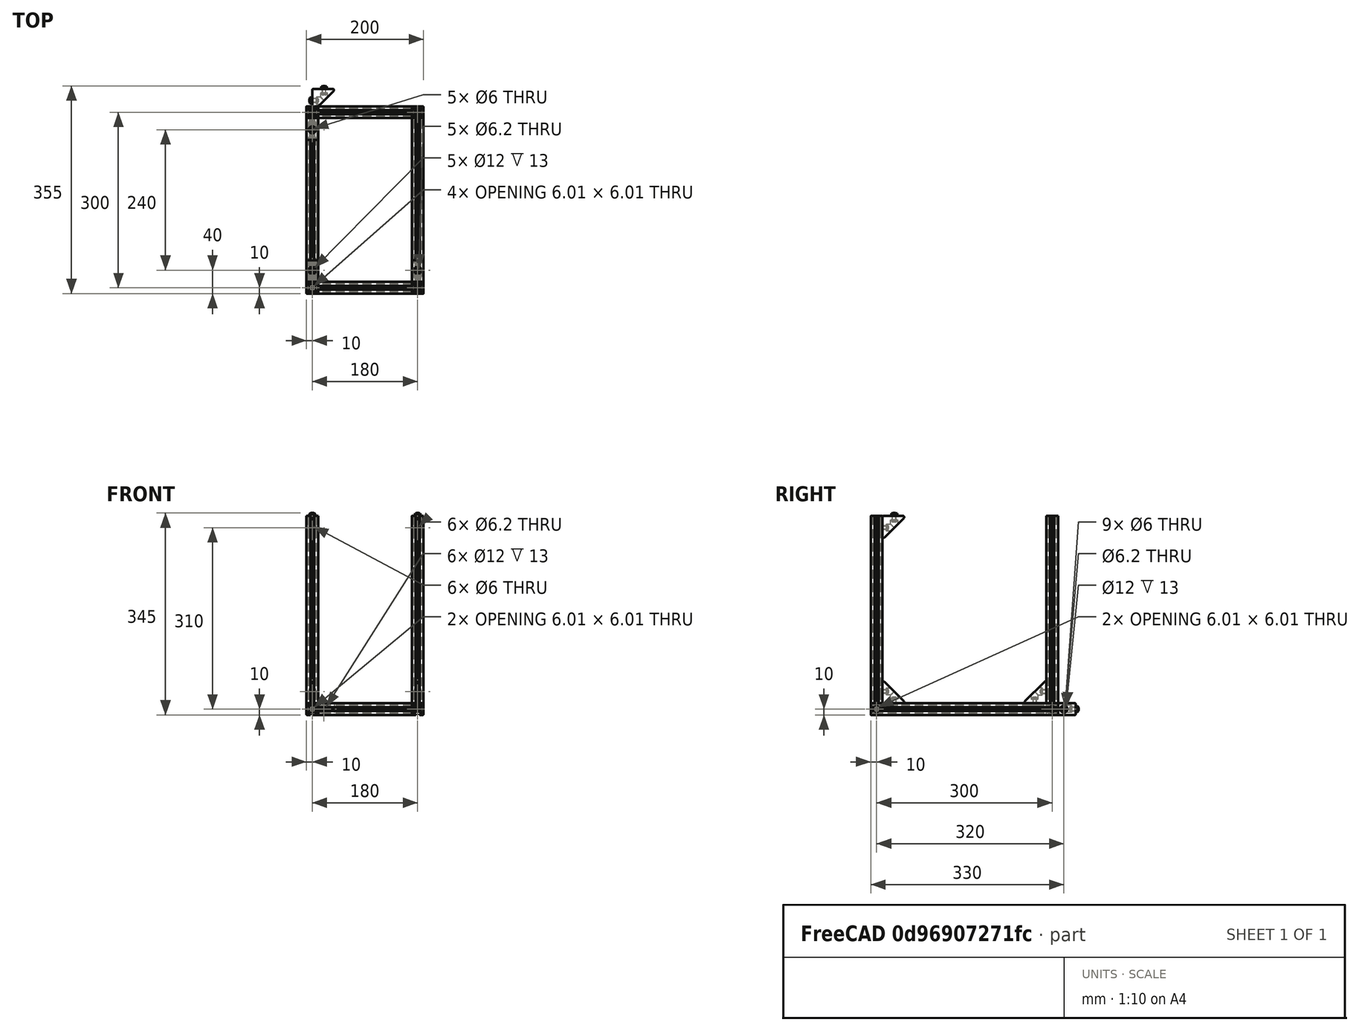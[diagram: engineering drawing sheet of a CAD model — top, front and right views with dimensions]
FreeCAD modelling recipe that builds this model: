
FCSTD DOCUMENT  (FreeCAD 0.17R9796 (Git))
Label: rawframeNG2b
License: All rights reserved
LicenseURL: http://en.wikipedia.org/wiki/All_rights_reserved
objects: Part::Feature×49, Part::FeaturePython×16, App::Part×6, Part::Compound×5
note: 70 computed .brp shape members not serialized (recipe doc carries the construction recipe); baked Part::Feature solids carry a one-line shape summary decoded from their .brp

FEATURE [Part::Feature] Pocket003001  label="tslot32con"
  Placement = pos=(0,10,10) rot=(1,0,0;1.5708rad)
  shape: bbox 20 x 320 x 20 mm, 150 faces (baked)
FEATURE [Part::Feature] Pocket003002  label="tslot16"
  Placement = pos=(10,0,10) rot=(0,1,0;1.5708rad)
  shape: bbox 160 x 20 x 20 mm, 94 faces (baked)
FEATURE [Part::Feature] Pocket003006  label="tslot16_001"
  Placement = pos=(10,-300,10) rot=(0,1,0;1.5708rad)
  shape: bbox 160 x 20 x 20 mm, 94 faces (baked)
FEATURE [Part::Feature] Pocket003007  label="tslot32con_001"
  Placement = pos=(180,-310,10) rot=(0,0.707107,0.707107;3.14159rad)
  shape: bbox 20 x 320 x 20 mm, 150 faces (baked)
FEATURE [Part::FeaturePython] Screw  label="M6x25-Screw"  # Fasteners workbench fastener (typed FeaturePython)
  Placement = pos=(-4,0,10) rot=(0,-1,0;1.5708rad)
  diameter = 7
  invert = false
  length = 6
  matchOuter = false
  offset = 0
  thread = false
  type = 15
FEATURE [Part::FeaturePython] Screw001  label="M6x25-Screw004"  # Fasteners workbench fastener (typed FeaturePython)
  Placement = pos=(-4,-300,10) rot=(0,-1,0;1.5708rad)
  diameter = 7
  invert = false
  length = 6
  matchOuter = false
  offset = 0
  thread = false
  type = 15
FEATURE [Part::FeaturePython] Screw002  label="M6x25-Screw005"  # Fasteners workbench fastener (typed FeaturePython)
  Placement = pos=(184,0,10) rot=(0,1,0;1.5708rad)
  diameter = 7
  invert = false
  length = 6
  matchOuter = false
  offset = 0
  thread = false
  type = 15
FEATURE [Part::FeaturePython] Screw004  label="M6x25-Screw006"  # Fasteners workbench fastener (typed FeaturePython)
  Placement = pos=(184,-300,10) rot=(0,1,0;1.5708rad)
  diameter = 7
  invert = false
  length = 6
  matchOuter = false
  offset = 0
  thread = false
  type = 15
FEATURE [App::Part] Part  label="lower_frame"
  Group = -> [Pocket003001,Pocket003002,Pocket003006,Pocket003007,Screw,Screw001,Screw002,Screw004]
  License = CC BY 3.0
  LicenseURL = http://creativecommons.org/licenses/by/3.0/
  Origin = -> PartOrigin
FEATURE [Part::Feature] Pocket003008  label="tslot32con001"
  Placement = pos=(0,10,10) rot=(1,0,0;1.5708rad)
  shape: bbox 20 x 320 x 20 mm, 150 faces (baked)
FEATURE [Part::Feature] Pocket003009  label="tslot041"
  Placement = pos=(10,0,10) rot=(0,1,0;1.5708rad)
  shape: bbox 160 x 20 x 20 mm, 94 faces (baked)
FEATURE [Part::Feature] Pocket003010  label="tslot16_002"
  Placement = pos=(10,-300,10) rot=(0,1,0;1.5708rad)
  shape: bbox 160 x 20 x 20 mm, 94 faces (baked)
FEATURE [Part::Feature] Pocket003011  label="tslot32con_002"
  Placement = pos=(180,-310,10) rot=(0,0.707107,0.707107;3.14159rad)
  shape: bbox 20 x 320 x 20 mm, 150 faces (baked)
FEATURE [Part::FeaturePython] Screw005  label="M6x25-Screw007"  # Fasteners workbench fastener (typed FeaturePython)
  Placement = pos=(-4,0,10) rot=(0,-1,0;1.5708rad)
  diameter = 7
  invert = false
  length = 6
  matchOuter = false
  offset = 0
  thread = false
  type = 15
FEATURE [Part::FeaturePython] Screw006  label="M6x25-Screw008"  # Fasteners workbench fastener (typed FeaturePython)
  Placement = pos=(-4,-300,10) rot=(0,-1,0;1.5708rad)
  diameter = 7
  invert = false
  length = 6
  matchOuter = false
  offset = 0
  thread = false
  type = 15
FEATURE [Part::FeaturePython] Screw007  label="M6x25-Screw009"  # Fasteners workbench fastener (typed FeaturePython)
  Placement = pos=(184,0,10) rot=(0,1,0;1.5708rad)
  diameter = 7
  invert = false
  length = 6
  matchOuter = false
  offset = 0
  thread = false
  type = 15
FEATURE [Part::FeaturePython] Screw008  label="M6x25-Screw010"  # Fasteners workbench fastener (typed FeaturePython)
  Placement = pos=(184,-300,10) rot=(0,1,0;1.5708rad)
  diameter = 7
  invert = false
  length = 6
  matchOuter = false
  offset = 0
  thread = false
  type = 15
FEATURE [App::Part] Part001  label="upper_frame"
  Group = -> [Pocket003008,Pocket003009,Pocket003010,Pocket003011,Screw005,Screw006,Screw007,Screw008]
  License = CC BY 3.0
  LicenseURL = http://creativecommons.org/licenses/by/3.0/
  Origin = -> PartOrigin001
  Placement = pos=(0,0,340) rot=(0,0,1;0rad)
FEATURE [Part::Feature] Fillet004001  label="Fillet005"
  shape: bbox 37.5 x 37.5 x 20 mm, 26 faces (baked)
FEATURE [Part::FeaturePython] Screw009  label="M6x12-Screw"  # Fasteners workbench fastener (typed FeaturePython)
  Placement = pos=(7,20,10) rot=(0,1,0;1.5708rad)
  diameter = 4
  invert = false
  length = 1
  matchOuter = false
  offset = 0
  thread = false
  type = 20
FEATURE [Part::Feature] Body001  label="m6nutplate"
  Placement = pos=(-1.5,15,5) rot=(0,-1,0;1.5708rad)
  shape: bbox 3 x 10 x 10 mm, 9 faces (baked)
FEATURE [App::Part] Part002  label="cornerstonescrewnut"
  License = CC BY 3.0
  LicenseURL = http://creativecommons.org/licenses/by/3.0/
  Origin = -> PartOrigin002
  Placement = pos=(10,-50,20) rot=(0,-1,0;1.5708rad)
FEATURE [Part::FeaturePython] Screw010  label="M6x12-Screw001"  # Fasteners workbench fastener (typed FeaturePython)
  Placement = pos=(20,33,10) rot=(1,0,0;1.5708rad)
  diameter = 4
  invert = false
  length = 1
  matchOuter = false
  offset = 0
  thread = false
  type = 20
FEATURE [Part::Feature] Body002  label="m6nutplate001"
  Placement = pos=(15,41.5,5) rot=(0.57735,0.57735,0.57735;4.18879rad)
  shape: bbox 10 x 3 x 10 mm, 9 faces (baked)
FEATURE [Part::Feature] Fillet004002  label="Fillet006"
  shape: bbox 37.5 x 37.5 x 20 mm, 26 faces (baked)
FEATURE [Part::FeaturePython] Screw011  label="M6x12-Screw002"  # Fasteners workbench fastener (typed FeaturePython)
  Placement = pos=(7,20,10) rot=(0,1,0;1.5708rad)
  diameter = 4
  invert = false
  length = 1
  matchOuter = false
  offset = 0
  thread = false
  type = 20
FEATURE [Part::Feature] Body003  label="m6nutplate002"
  Placement = pos=(-1.5,15,5) rot=(0,-1,0;1.5708rad)
  shape: bbox 3 x 10 x 10 mm, 9 faces (baked)
FEATURE [Part::FeaturePython] Screw012  label="M6x12-Screw003"  # Fasteners workbench fastener (typed FeaturePython)
  Placement = pos=(20,33,10) rot=(1,0,0;1.5708rad)
  diameter = 4
  invert = false
  length = 1
  matchOuter = false
  offset = 0
  thread = false
  type = 20
FEATURE [Part::Feature] Body004  label="m6nutplate003"
  Placement = pos=(15,41.5,5) rot=(0.57735,0.57735,0.57735;4.18879rad)
  shape: bbox 10 x 3 x 10 mm, 9 faces (baked)
FEATURE [App::Part] Part003  label="cornerstonescrewnut001"
  Group = -> [Body003,Screw011,Fillet004002,Screw012,Body004,PartOrigin002,Body001,Screw009,Fillet004001,Screw010,Body002,Part002]
  License = CC BY 3.0
  LicenseURL = http://creativecommons.org/licenses/by/3.0/
  Origin = -> PartOrigin003
  Placement = pos=(190,-50,20) rot=(0,-1,0;1.5708rad)
FEATURE [Part::Feature] Fillet004003  label="Fillet007"
  shape: bbox 37.5 x 37.5 x 20 mm, 26 faces (baked)
FEATURE [Part::FeaturePython] Screw013  label="M6x12-Screw004"  # Fasteners workbench fastener (typed FeaturePython)
  Placement = pos=(7,20,10) rot=(0,1,0;1.5708rad)
  diameter = 4
  invert = false
  length = 1
  matchOuter = false
  offset = 0
  thread = false
  type = 20
FEATURE [Part::Feature] Body005  label="m6nutplate004"
  Placement = pos=(-1.5,15,5) rot=(0,-1,0;1.5708rad)
  shape: bbox 3 x 10 x 10 mm, 9 faces (baked)
FEATURE [Part::FeaturePython] Screw014  label="M6x12-Screw005"  # Fasteners workbench fastener (typed FeaturePython)
  Placement = pos=(20,33,10) rot=(1,0,0;1.5708rad)
  diameter = 4
  invert = false
  length = 1
  matchOuter = false
  offset = 0
  thread = false
  type = 20
FEATURE [Part::Feature] Body006  label="m6nutplate005"
  Placement = pos=(15,41.5,5) rot=(0.57735,0.57735,0.57735;4.18879rad)
  shape: bbox 10 x 3 x 10 mm, 9 faces (baked)
FEATURE [App::Part] Part004  label="cornerstonescrewnut002"
  Group = -> [Body005,Screw013,Fillet004003,Screw014,Body006]
  License = CC BY 3.0
  LicenseURL = http://creativecommons.org/licenses/by/3.0/
  Origin = -> PartOrigin004
  Placement = pos=(-10,-50,340) rot=(0,1,0;1.5708rad)
FEATURE [Part::Feature] Fillet004004  label="Fillet008"
  shape: bbox 37.5 x 37.5 x 20 mm, 26 faces (baked)
FEATURE [Part::FeaturePython] Screw015  label="M6x12-Screw006"  # Fasteners workbench fastener (typed FeaturePython)
  Placement = pos=(7,20,10) rot=(0,1,0;1.5708rad)
  diameter = 4
  invert = false
  length = 1
  matchOuter = false
  offset = 0
  thread = false
  type = 20
FEATURE [Part::Feature] Body007  label="m6nutplate006"
  Placement = pos=(-1.5,15,5) rot=(0,-1,0;1.5708rad)
  shape: bbox 3 x 10 x 10 mm, 9 faces (baked)
FEATURE [Part::FeaturePython] Screw016  label="M6x12-Screw007"  # Fasteners workbench fastener (typed FeaturePython)
  Placement = pos=(20,33,10) rot=(1,0,0;1.5708rad)
  diameter = 4
  invert = false
  length = 1
  matchOuter = false
  offset = 0
  thread = false
  type = 20
FEATURE [Part::Feature] Body008  label="m6nutplate007"
  Placement = pos=(15,41.5,5) rot=(0.57735,0.57735,0.57735;4.18879rad)
  shape: bbox 10 x 3 x 10 mm, 9 faces (baked)
FEATURE [App::Part] Part005  label="cornerstonescrewnut003"
  Group = -> [Body007,Screw015,Fillet004004,Screw016,Body008]
  License = CC BY 3.0
  LicenseURL = http://creativecommons.org/licenses/by/3.0/
  Origin = -> PartOrigin005
  Placement = pos=(170,-50,340) rot=(0,1,0;1.5708rad)
FEATURE [Part::Feature] Body009001  label="m6nutplate010"
  Placement = pos=(-1.5,15,5) rot=(0,-1,0;1.5708rad)
  shape: bbox 3 x 10 x 10 mm, 9 faces (baked)
FEATURE [Part::Feature] Body010001  label="m6nutplate011"
  Placement = pos=(15,41.5,5) rot=(0.57735,0.57735,0.57735;4.18879rad)
  shape: bbox 10 x 3 x 10 mm, 9 faces (baked)
FEATURE [Part::Feature] Screw018001  label="M6x12-Screw010"
  Placement = pos=(20,33,10) rot=(1,0,0;1.5708rad)
  shape: bbox 10.5 x 15.3 x 10.5 mm, 15 faces (baked)
FEATURE [Part::Feature] Screw017001  label="M6x12-Screw011"
  Placement = pos=(7,20,10) rot=(0,1,0;1.5708rad)
  shape: bbox 15.3 x 10.5 x 10.5 mm, 15 faces (baked)
FEATURE [Part::Feature] Fillet004005001  label="Fillet010"
  shape: bbox 37.5 x 37.5 x 20 mm, 26 faces (baked)
FEATURE [Part::Compound] Compound
  Links = -> [Body009001,Fillet004005001,Screw017001,Body010001,Screw018001]
  Placement = pos=(10,-250,340) rot=(0.707107,0,-0.707107;3.14159rad)
FEATURE [Part::Feature] Body010002  label="m6nutplate012"
  Placement = pos=(-1.5,15,5) rot=(0,-1,0;1.5708rad)
  shape: bbox 3 x 10 x 10 mm, 9 faces (baked)
FEATURE [Part::Feature] Body010003  label="m6nutplate013"
  Placement = pos=(15,41.5,5) rot=(0.57735,0.57735,0.57735;4.18879rad)
  shape: bbox 10 x 3 x 10 mm, 9 faces (baked)
FEATURE [Part::Feature] Screw018002  label="M6x12-Screw012"
  Placement = pos=(20,33,10) rot=(1,0,0;1.5708rad)
  shape: bbox 10.5 x 15.3 x 10.5 mm, 15 faces (baked)
FEATURE [Part::Feature] Screw018003  label="M6x12-Screw013"
  Placement = pos=(7,20,10) rot=(0,1,0;1.5708rad)
  shape: bbox 15.3 x 10.5 x 10.5 mm, 15 faces (baked)
FEATURE [Part::Feature] Fillet004005002  label="Fillet011"
  shape: bbox 37.5 x 37.5 x 20 mm, 26 faces (baked)
FEATURE [Part::Compound] Compound001
  Links = -> [Body010002,Fillet004005002,Screw018003,Body010003,Screw018002]
  Placement = pos=(190,-250,340) rot=(0.707107,0,-0.707107;3.14159rad)
FEATURE [Part::Feature] Body010004  label="m6nutplate014"
  Placement = pos=(-1.5,15,5) rot=(0,-1,0;1.5708rad)
  shape: bbox 3 x 10 x 10 mm, 9 faces (baked)
FEATURE [Part::Feature] Body010005  label="m6nutplate015"
  Placement = pos=(15,41.5,5) rot=(0.57735,0.57735,0.57735;4.18879rad)
  shape: bbox 10 x 3 x 10 mm, 9 faces (baked)
FEATURE [Part::Feature] Screw018004  label="M6x12-Screw014"
  Placement = pos=(20,33,10) rot=(1,0,0;1.5708rad)
  shape: bbox 10.5 x 15.3 x 10.5 mm, 15 faces (baked)
FEATURE [Part::Feature] Screw018005  label="M6x12-Screw015"
  Placement = pos=(7,20,10) rot=(0,1,0;1.5708rad)
  shape: bbox 15.3 x 10.5 x 10.5 mm, 15 faces (baked)
FEATURE [Part::Feature] Fillet004005003  label="Fillet012"
  shape: bbox 37.5 x 37.5 x 20 mm, 26 faces (baked)
FEATURE [Part::Compound] Compound002
  Links = -> [Body010004,Fillet004005003,Screw018005,Body010005,Screw018004]
  Placement = pos=(10,-290,60) rot=(0.57735,0.57735,-0.57735;4.18879rad)
FEATURE [Part::Feature] Body010006  label="m6nutplate016"
  Placement = pos=(-1.5,15,5) rot=(0,-1,0;1.5708rad)
  shape: bbox 3 x 10 x 10 mm, 9 faces (baked)
FEATURE [Part::Feature] Body010007  label="m6nutplate017"
  Placement = pos=(15,41.5,5) rot=(0.57735,0.57735,0.57735;4.18879rad)
  shape: bbox 10 x 3 x 10 mm, 9 faces (baked)
FEATURE [Part::Feature] Screw018006  label="M6x12-Screw016"
  Placement = pos=(20,33,10) rot=(1,0,0;1.5708rad)
  shape: bbox 10.5 x 15.3 x 10.5 mm, 15 faces (baked)
FEATURE [Part::Feature] Screw018007  label="M6x12-Screw017"
  Placement = pos=(7,20,10) rot=(0,1,0;1.5708rad)
  shape: bbox 15.3 x 10.5 x 10.5 mm, 15 faces (baked)
FEATURE [Part::Feature] Fillet004005004  label="Fillet013"
  shape: bbox 37.5 x 37.5 x 20 mm, 26 faces (baked)
FEATURE [Part::Compound] Compound003
  Links = -> [Body010006,Fillet004005004,Screw018007,Body010007,Screw018006]
  Placement = pos=(190,-290,60) rot=(0.57735,0.57735,-0.57735;4.18879rad)
FEATURE [Part::Feature] Pocket001001  label="tslot32"
  Placement = pos=(0,0,20) rot=(0,0,1;0rad)
  shape: bbox 20 x 20 x 320 mm, 94 faces (baked)
FEATURE [Part::Feature] Body010008  label="m6nutplate018"
  Placement = pos=(-1.5,15,5) rot=(0,-1,0;1.5708rad)
  shape: bbox 3 x 10 x 10 mm, 9 faces (baked)
FEATURE [Part::Feature] Body010009  label="m6nutplate019"
  Placement = pos=(15,41.5,5) rot=(0.57735,0.57735,0.57735;4.18879rad)
  shape: bbox 10 x 3 x 10 mm, 9 faces (baked)
FEATURE [Part::Feature] Screw018008  label="M6x12-Screw018"
  Placement = pos=(20,33,10) rot=(1,0,0;1.5708rad)
  shape: bbox 10.5 x 15.3 x 10.5 mm, 15 faces (baked)
FEATURE [Part::Feature] Screw018009  label="M6x12-Screw019"
  Placement = pos=(7,20,10) rot=(0,1,0;1.5708rad)
  shape: bbox 15.3 x 10.5 x 10.5 mm, 15 faces (baked)
FEATURE [Part::Feature] Fillet004005005  label="Fillet014"
  shape: bbox 37.5 x 37.5 x 20 mm, 26 faces (baked)
FEATURE [Part::Compound] Compound004
  Links = -> [Body010008,Fillet004005005,Screw018009,Body010009,Screw018008]
  Placement = pos=(-10,-10,60) rot=(0.57735,-0.57735,0.57735;4.18879rad)
FEATURE [Part::Feature] Pocket003012  label="tslot32_001"
  Placement = pos=(0,-300,20) rot=(0,0,1;0rad)
  shape: bbox 20 x 20 x 320 mm, 94 faces (baked)
FEATURE [Part::Feature] Pocket003013  label="tslot32_002"
  Placement = pos=(180,0,20) rot=(0,0,1;0rad)
  shape: bbox 20 x 20 x 320 mm, 94 faces (baked)
FEATURE [Part::Feature] Pocket003014  label="tslot32_003"
  Placement = pos=(180,-300,20) rot=(0,0,1;0rad)
  shape: bbox 20 x 20 x 320 mm, 94 faces (baked)
